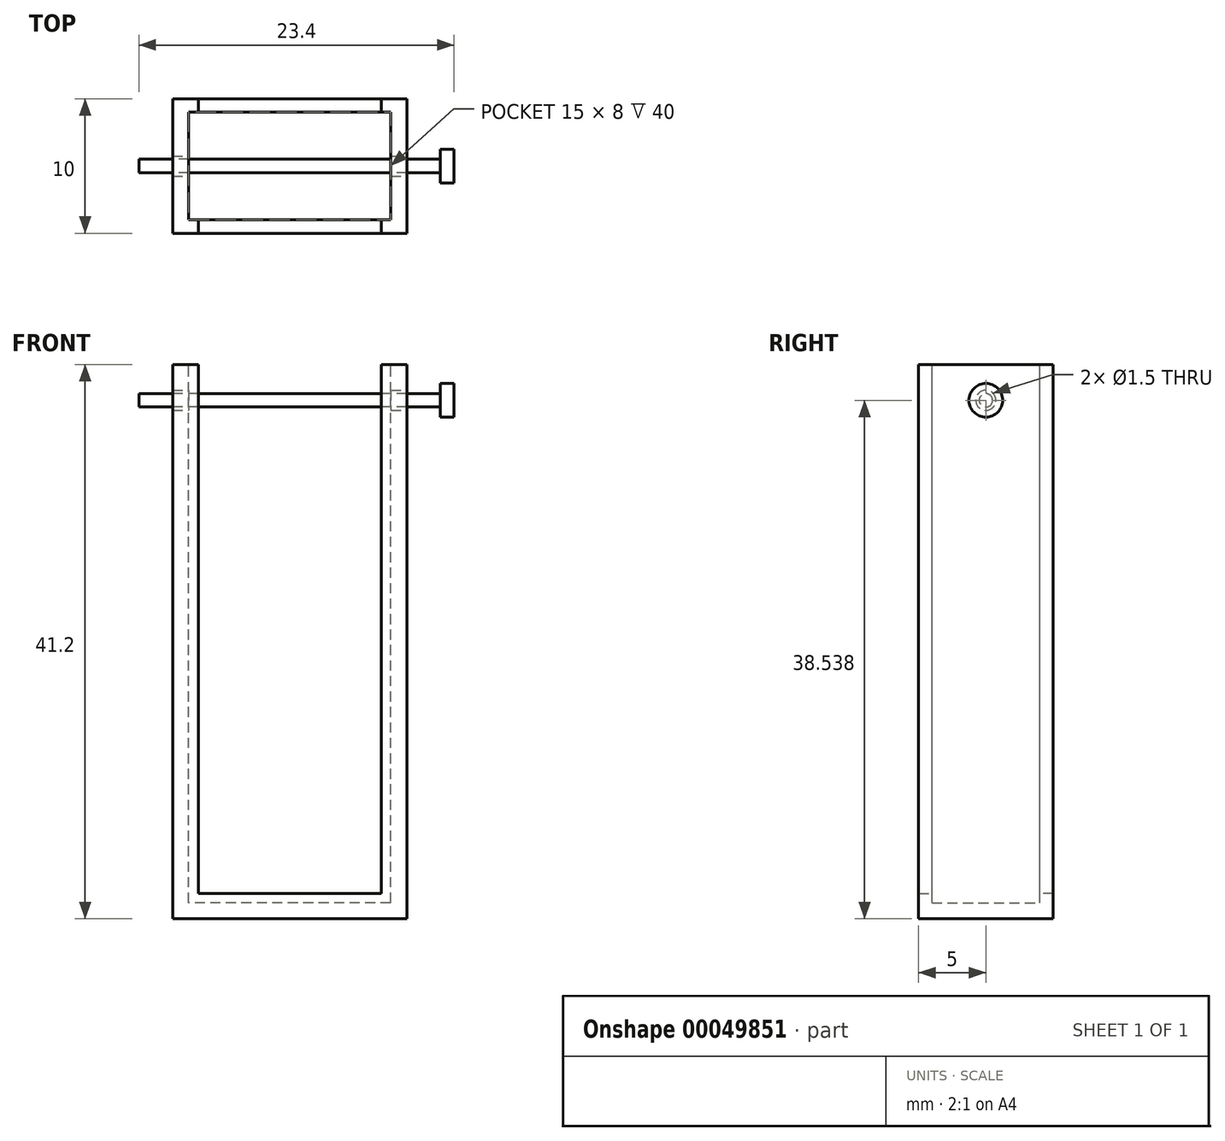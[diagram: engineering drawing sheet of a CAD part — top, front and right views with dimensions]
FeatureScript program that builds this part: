
annotation { "Feature Type Name" : "Feature", "Feature Type Description" : "" }
export const myFeature = defineFeature(function(context is Context, id is Id, definition is map)
    precondition{}
    {
        {
            var Q0;
            Q0=qCreatedBy(makeId("Front.planeOp"),FACE);
            var sketch = newSketch(context, id + "F0", { "sketchPlane" : qUnion([Q0])});
            skLineSegment(sketch, "E0.bottom", {"start": v(7.5, -20) * mm, "end": v(-7.5, -20) * mm});
            skLineSegment(sketch, "E0.top", {"start": v(7.5, 20) * mm, "end": v(-7.5, 20) * mm});
            skLineSegment(sketch, "E0.left", {"start": v(7.5, -20) * mm, "end": v(7.5, 20) * mm});
            skLineSegment(sketch, "E0.right", {"start": v(-7.5, -20) * mm, "end": v(-7.5, 20) * mm});
            skPoint(sketch, "E0.middle", {"position": v(0, 0) * mm});
            skLineSegment(sketch, "E1.0", {"start": v(8.7, -21.2) * mm, "end": v(8.7, 20) * mm});
            skLineSegment(sketch, "E1.1", {"start": v(8.7, -21.2) * mm, "end": v(-8.7, -21.2) * mm});
            skLineSegment(sketch, "E1.2", {"start": v(-8.7, -21.2) * mm, "end": v(-8.7, 20) * mm});
            skLineSegment(sketch, "E2", {"start": v(-7.5, 20) * mm, "end": v(-8.7, 20) * mm});
            skLineSegment(sketch, "E3", {"start": v(7.5, 20) * mm, "end": v(8.7, 20) * mm});
            skLineSegment(sketch, "E4.0", {"start": v(6.8, -19.3) * mm, "end": v(6.8, 20) * mm});
            skLineSegment(sketch, "E4.1", {"start": v(6.8, -19.3) * mm, "end": v(-6.8, -19.3) * mm});
            skLineSegment(sketch, "E4.2", {"start": v(-6.8, -19.3) * mm, "end": v(-6.8, 20) * mm});
            skSolve(sketch);
        }
        {
            var Q0;
            Q0=makeQuery(id+"F0.imprint","IMPRINT",FACE,{"disambiguationData":[TD([[makeQuery(id+"F0.imprint","IMPRINT",EDGE,{"derivedFrom":sQuery(id+"F0.wireOp",EDGE,"E0.bottom")}),1.0]])]});
            extrude(context, id + "F1", {"entities" : qUnion([Q0]), "depth" : 4 * mm, "hasSecondDirection" : true, "secondDirectionOppositeDirection" : true, "secondDirectionDepth" : 4 * mm});
        }
        {
            var Q0;
            Q0=makeQuery(id+"F0.imprint","IMPRINT",FACE,{"disambiguationData":[TD([[makeQuery(id+"F0.imprint","IMPRINT",EDGE,{"derivedFrom":sQuery(id+"F0.wireOp",EDGE,"E0.bottom")}),-1.0]])]});
            var Q1;
            Q1=makeQuery(id+"F0.imprint","IMPRINT",FACE,{"disambiguationData":[TD([[makeQuery(id+"F0.imprint","IMPRINT",EDGE,{"derivedFrom":sQuery(id+"F0.wireOp",EDGE,"E0.bottom")}),1.0]])]});
            extrude(context, id + "F2", {"entities" : qUnion([Q0, Q1]), "operationType" : NewBodyOperationType.ADD, "oppositeDirection" : true, "depth" : 5 * mm, "hasSecondDirection" : true, "secondDirectionOppositeDirection" : true, "secondDirectionDepth" : 4 * mm});
        }
        {
            var Q0;
            Q0=makeQuery(id+"F0.imprint","IMPRINT",FACE,{"disambiguationData":[TD([[makeQuery(id+"F0.imprint","IMPRINT",EDGE,{"derivedFrom":sQuery(id+"F0.wireOp",EDGE,"E0.bottom")}),1.0]])]});
            var Q1;
            Q1=makeQuery(id+"F0.imprint","IMPRINT",FACE,{"disambiguationData":[TD([[makeQuery(id+"F0.imprint","IMPRINT",EDGE,{"derivedFrom":sQuery(id+"F0.wireOp",EDGE,"E0.bottom")}),-1.0]])]});
            extrude(context, id + "F3", {"entities" : qUnion([Q0, Q1]), "operationType" : NewBodyOperationType.ADD, "depth" : 5 * mm, "hasSecondDirection" : true, "secondDirectionOppositeDirection" : false, "secondDirectionDepth" : 4 * mm});
        }
        {
            var Q0;
            {var subQ0=sQuery(id+"F0.wireOp",EDGE,"E1.0");Q0=makeQuery(id+"F3.boolean.opBoolean","MERGE",FACE,{"derivedFrom":[makeQuery(id+"F2.boolean.opBoolean","MERGE",FACE,{"derivedFrom":[makeQuery(id+"F1.opExtrude","SWEPT_FACE",FACE,{"disambiguationData":[OSD([subQ0])]}),makeQuery(id+"F2.opExtrude","SWEPT_FACE",FACE,{"disambiguationData":[OSD([subQ0])]})]}),makeQuery(id+"F3.opExtrude","SWEPT_FACE",FACE,{"disambiguationData":[OSD([subQ0])]})]});}
            var sketch = newSketch(context, id + "F4", { "sketchPlane" : qUnion([Q0])});
            skCircle(sketch, "E5", {"center": v(0, 17.34) * mm, "radius": 0.75 * mm});
            skCircle(sketch, "E6", {"center": v(0, 17.34) * mm, "radius": 0.5 * mm});
            skCircle(sketch, "E7", {"center": v(0, 17.34) * mm, "radius": 1.25 * mm});
            skSolve(sketch);
        }
        {
            var Q0;
            Q0=makeQuery(id+"F4.imprint","IMPRINT",FACE,{"disambiguationData":[TD([[makeQuery(id+"F4.imprint","IMPRINT",EDGE,{"derivedFrom":sQuery(id+"F4.wireOp",EDGE,"E5")}),1.0]])]});
            var Q1;
            {var subQ0=sQuery(id+"F4.wireOp",EDGE,"E6");var subQ1=makeQuery(id+"F4.imprint","INTERSECT",VERTEX,{"derivedFrom":[subQ0,sQuery(id+"F4.wireOp",EDGE,"4A9cRJv5-mFtq-hMWj-Mfol-3ztwxUiiXE9g.bottom")]});Q1=makeQuery(id+"F4.imprint","IMPRINT",FACE,{"disambiguationData":[TD([[makeQuery(id+"F4.imprint","IMPRINT",EDGE,{"disambiguationData":[TD([[subQ1,-1.0]])],"derivedFrom":subQ0}),1.0]])]});}
            var Q2;
            {var subQ0=sQuery(id+"F4.wireOp",EDGE,"4A9cRJv5-mFtq-hMWj-Mfol-3ztwxUiiXE9g.bottom");var subQ1=sQuery(id+"F4.wireOp",EDGE,"E5");var subQ2=makeQuery(id+"F4.imprint","INTERSECT",VERTEX,{"disambiguationData":[OD(1.0)],"derivedFrom":[subQ1,subQ0]});Q2=makeQuery(id+"F4.imprint","IMPRINT",FACE,{"disambiguationData":[TD([[makeQuery(id+"F4.imprint","IMPRINT",EDGE,{"disambiguationData":[TD([[subQ2,1.0]])],"derivedFrom":subQ1}),1.0]])]});}
            var Q3;
            {var subQ0=sQuery(id+"F4.wireOp",EDGE,"4A9cRJv5-mFtq-hMWj-Mfol-3ztwxUiiXE9g.bottom");var subQ1=sQuery(id+"F4.wireOp",EDGE,"E5");var subQ2=makeQuery(id+"F4.imprint","INTERSECT",VERTEX,{"disambiguationData":[OD(0.0)],"derivedFrom":[subQ1,subQ0]});Q3=makeQuery(id+"F4.imprint","IMPRINT",FACE,{"disambiguationData":[TD([[makeQuery(id+"F4.imprint","IMPRINT",EDGE,{"disambiguationData":[TD([[subQ2,-1.0]])],"derivedFrom":subQ1}),1.0]])]});}
            extrude(context, id + "F5", {"entities" : qUnion([Q0, Q1, Q2, Q3]), "operationType" : NewBodyOperationType.REMOVE, "oppositeDirection" : true, "depth" : 25 * mm});
        }
        {
            var Q0;
            Q0=makeQuery(id+"F4.imprint","IMPRINT",FACE,{"disambiguationData":[TD([[makeQuery(id+"F4.imprint","IMPRINT",EDGE,{"derivedFrom":sQuery(id+"F4.wireOp",EDGE,"E6")}),1.0]])]});
            extrude(context, id + "F6", {"entities" : qUnion([Q0]), "depth" : 2.5 * mm, "hasSecondDirection" : true, "secondDirectionOppositeDirection" : true, "secondDirectionDepth" : (17.4 + 2.5) * mm});
        }
        {
            var Q0;
            Q0=makeQuery(id+"F4.imprint","IMPRINT",FACE,{"disambiguationData":[TD([[makeQuery(id+"F4.imprint","IMPRINT",EDGE,{"derivedFrom":sQuery(id+"F4.wireOp",EDGE,"E6")}),1.0]])]});
            var Q1;
            Q1=makeQuery(id+"F4.imprint","IMPRINT",FACE,{"disambiguationData":[TD([[makeQuery(id+"F4.imprint","IMPRINT",EDGE,{"derivedFrom":sQuery(id+"F4.wireOp",EDGE,"E5")}),1.0]])]});
            var Q2;
            Q2=makeQuery(id+"F4.imprint","IMPRINT",FACE,{"disambiguationData":[TD([[makeQuery(id+"F4.imprint","IMPRINT",EDGE,{"derivedFrom":sQuery(id+"F4.wireOp",EDGE,"E5")}),-1.0]])]});
            extrude(context, id + "F7", {"entities" : qUnion([Q0, Q1, Q2]), "operationType" : NewBodyOperationType.ADD, "depth" : 3.5 * mm, "hasSecondDirection" : true, "secondDirectionOppositeDirection" : false, "secondDirectionDepth" : 2.5 * mm});
        }
    });
